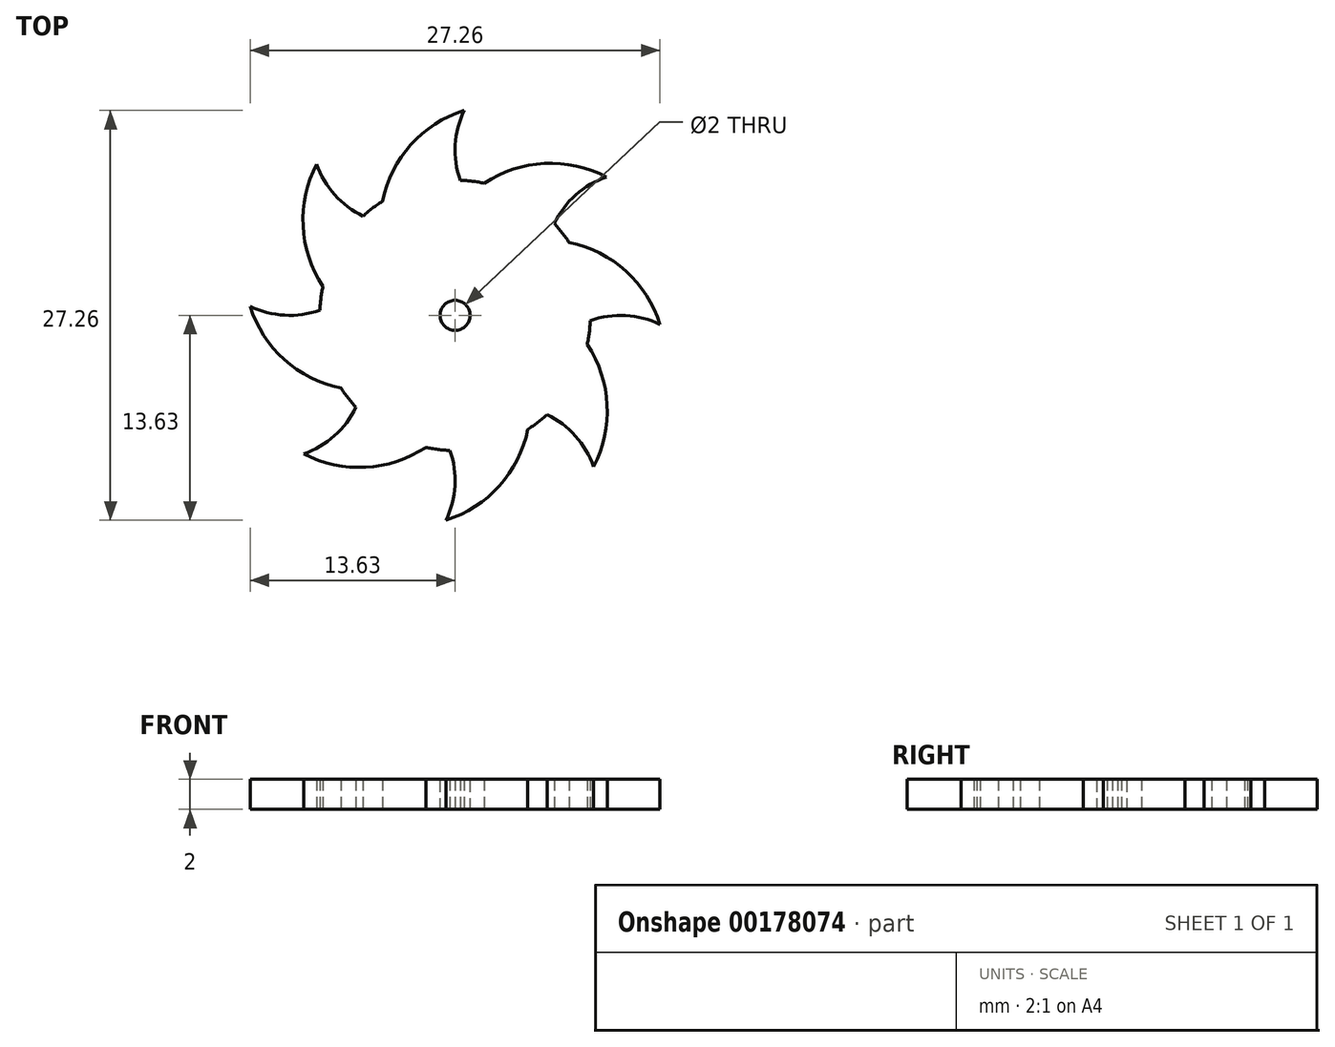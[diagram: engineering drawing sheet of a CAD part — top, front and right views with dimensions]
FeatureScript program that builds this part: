
annotation { "Feature Type Name" : "Feature", "Feature Type Description" : "" }
export const myFeature = defineFeature(function(context is Context, id is Id, definition is map)
    precondition{}
    {
        {
            var Q0;
            Q0=qCreatedBy(makeId("Top.planeOp"),FACE);
            var sketch = newSketch(context, id + "F0", { "sketchPlane" : qUnion([Q0])});
            skCircle(sketch, "E0", {"center": v(0, 0) * mm, "radius": 9 * mm});
            skLineSegment(sketch, "E1", {"start": v(0, 0) * mm, "end": v(0, 9) * mm, "construction": true});
            skArc(sketch, "E2", {"start": v(0.6, 13.63) * mm, "mid": v(-2.94, 11.36) * mm, "end": v(-4.84, 7.59) * mm});
            skArc(sketch, "E3", {"start": v(0.6, 13.63) * mm, "mid": v(0, 11.34) * mm, "end": v(0.35, 9) * mm});
            skArc(sketch, "E4.1.0", {"start": v(-9.21, 10.07) * mm, "mid": v(-10.11, 5.95) * mm, "end": v(-8.79, 1.94) * mm});
            skArc(sketch, "E4.1.1", {"start": v(-9.21, 10.07) * mm, "mid": v(-8.01, 8.03) * mm, "end": v(-6.11, 6.6) * mm});
            skArc(sketch, "E4.2.0", {"start": v(-13.63, 0.6) * mm, "mid": v(-11.36, -2.94) * mm, "end": v(-7.59, -4.84) * mm});
            skArc(sketch, "E4.2.1", {"start": v(-13.63, 0.6) * mm, "mid": v(-11.34, 0) * mm, "end": v(-9, 0.35) * mm});
            skArc(sketch, "E4.3.0", {"start": v(-10.07, -9.21) * mm, "mid": v(-5.95, -10.11) * mm, "end": v(-1.94, -8.79) * mm});
            skArc(sketch, "E4.3.1", {"start": v(-10.07, -9.21) * mm, "mid": v(-8.03, -8.01) * mm, "end": v(-6.6, -6.11) * mm});
            skArc(sketch, "E4.4.0", {"start": v(-0.6, -13.63) * mm, "mid": v(2.94, -11.36) * mm, "end": v(4.84, -7.59) * mm});
            skArc(sketch, "E4.4.1", {"start": v(-0.6, -13.63) * mm, "mid": v(0, -11.34) * mm, "end": v(-0.35, -9) * mm});
            skArc(sketch, "E5.3.5.0", {"start": v(9.21, -10.07) * mm, "mid": v(10.11, -5.95) * mm, "end": v(8.79, -1.94) * mm});
            skArc(sketch, "E5.4.5.0", {"start": v(9.21, -10.07) * mm, "mid": v(8.01, -8.03) * mm, "end": v(6.11, -6.6) * mm});
            skArc(sketch, "E5.3.6.0", {"start": v(13.63, -0.6) * mm, "mid": v(11.36, 2.94) * mm, "end": v(7.59, 4.84) * mm});
            skArc(sketch, "E5.4.6.0", {"start": v(13.63, -0.6) * mm, "mid": v(11.34, 0) * mm, "end": v(9, -0.35) * mm});
            skArc(sketch, "E5.3.7.0", {"start": v(10.07, 9.21) * mm, "mid": v(5.95, 10.11) * mm, "end": v(1.94, 8.79) * mm});
            skArc(sketch, "E5.4.7.0", {"start": v(10.07, 9.21) * mm, "mid": v(8.03, 8.01) * mm, "end": v(6.6, 6.11) * mm});
            skSolve(sketch);
        }
        {
            var Q0;
            Q0=qSketchRegion(id+"F0",true);
            extrude(context, id + "F1", {"entities" : qUnion([Q0]), "depth" : 2 * mm});
        }
        {
            var Q0;
            Q0=makeQuery(id+"F1.opExtrude","CAP_FACE",FACE,{"disambiguationData":[OSD([sQuery(id+"F0.wireOp",EDGE,"E0"),sQuery(id+"F0.wireOp",EDGE,"E2"),sQuery(id+"F0.wireOp",EDGE,"E3"),sQuery(id+"F0.wireOp",EDGE,"E4.1.0"),sQuery(id+"F0.wireOp",EDGE,"E4.1.1"),sQuery(id+"F0.wireOp",EDGE,"E4.2.0"),sQuery(id+"F0.wireOp",EDGE,"E4.2.1"),sQuery(id+"F0.wireOp",EDGE,"E4.3.0"),sQuery(id+"F0.wireOp",EDGE,"E4.3.1"),sQuery(id+"F0.wireOp",EDGE,"E4.4.0"),sQuery(id+"F0.wireOp",EDGE,"E4.4.1")])],"isStart":false});
            var sketch = newSketch(context, id + "F2", { "sketchPlane" : qUnion([Q0])});
            skCircle(sketch, "E6", {"center": v(0, 0) * mm, "radius": 1 * mm});
            skSolve(sketch);
        }
        {
            var Q0;
            Q0=qSketchRegion(id+"F2",true);
            extrude(context, id + "F3", {"entities" : qUnion([Q0]), "operationType" : NewBodyOperationType.REMOVE, "endBound" : BoundingType.THROUGH_ALL, "oppositeDirection" : true, "depth" : 25 * mm});
        }
    });
